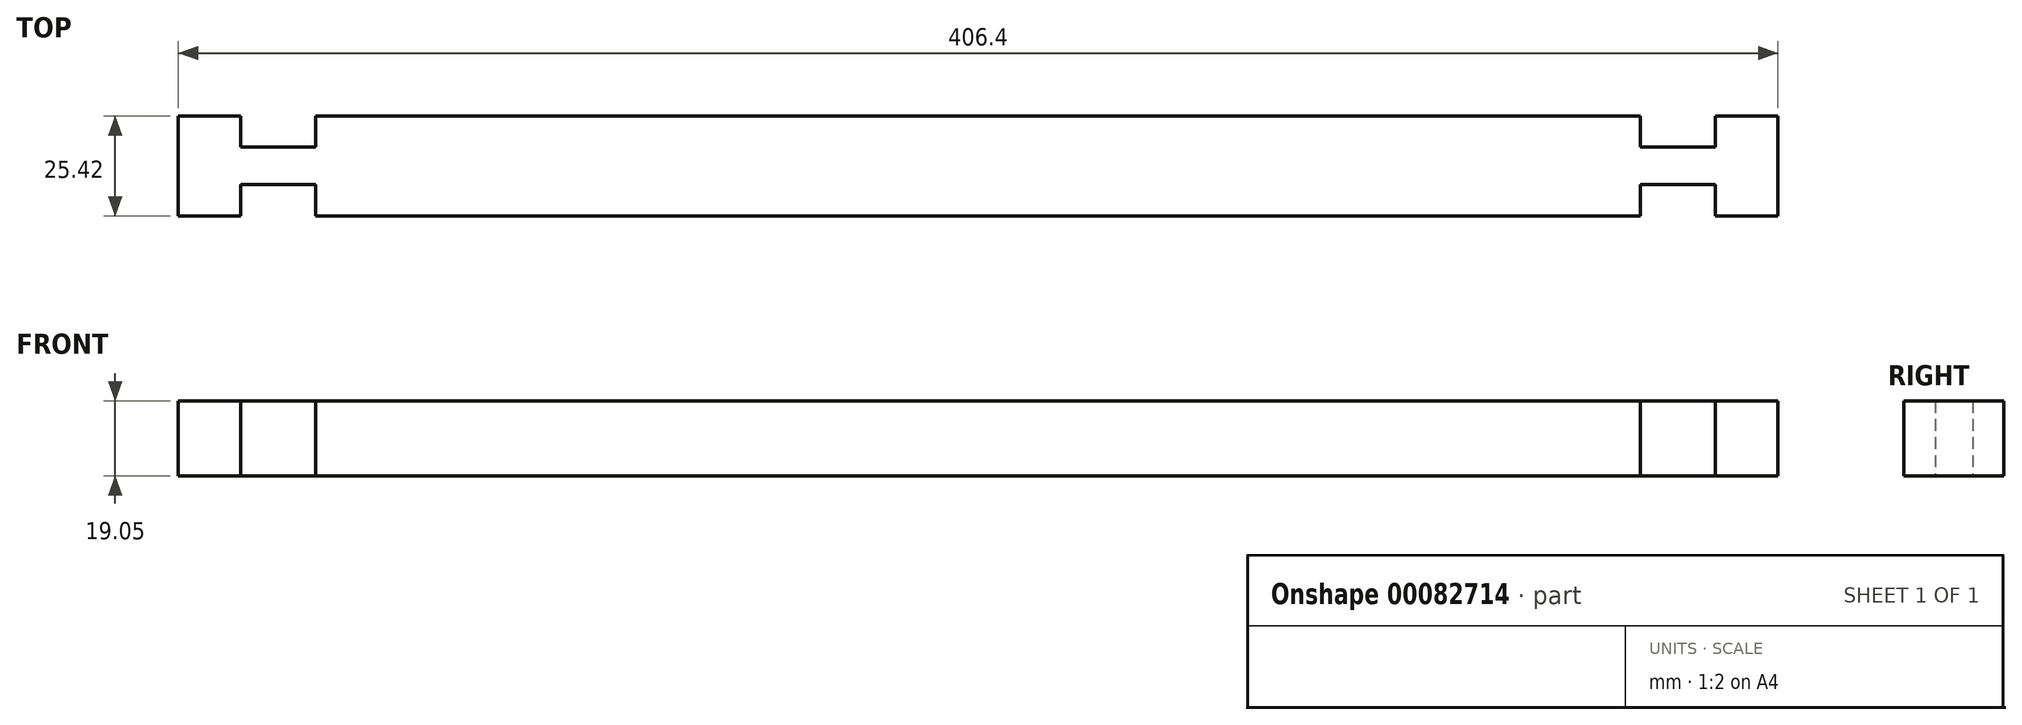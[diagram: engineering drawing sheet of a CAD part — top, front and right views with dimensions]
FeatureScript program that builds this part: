
annotation { "Feature Type Name" : "Feature", "Feature Type Description" : "" }
export const myFeature = defineFeature(function(context is Context, id is Id, definition is map)
    precondition{}
    {
        {
            var Q0;
            Q0=qCreatedBy(makeId("Top.planeOp"),FACE);
            var sketch = newSketch(context, id + "F0", { "sketchPlane" : qUnion([Q0])});
            skLineSegment(sketch, "E0", {"start": v(3.6, 15.79) * mm, "end": v(19.48, 15.79) * mm});
            skLineSegment(sketch, "E1", {"start": v(19.48, 15.79) * mm, "end": v(19.48, 23.73) * mm});
            skLineSegment(sketch, "E2", {"start": v(19.48, 23.73) * mm, "end": v(38.53, 23.73) * mm});
            skLineSegment(sketch, "E3", {"start": v(38.53, 23.73) * mm, "end": v(38.53, 15.78) * mm});
            skLineSegment(sketch, "E4", {"start": v(38.53, 15.78) * mm, "end": v(375.08, 15.78) * mm});
            skLineSegment(sketch, "E5", {"start": v(375.08, 15.78) * mm, "end": v(375.08, 23.73) * mm});
            skLineSegment(sketch, "E6", {"start": v(375.08, 23.73) * mm, "end": v(394.13, 23.73) * mm});
            skLineSegment(sketch, "E7", {"start": v(394.13, 23.73) * mm, "end": v(394.13, 15.78) * mm});
            skLineSegment(sketch, "E8", {"start": v(3.6, 15.79) * mm, "end": v(3.6, 28.49) * mm});
            skLineSegment(sketch, "E9", {"start": v(3.6, 41.19) * mm, "end": v(3.6, 28.49) * mm});
            skLineSegment(sketch, "E10.MirrorCS", {"start": v(19.48, 33.25) * mm, "end": v(38.53, 33.25) * mm});
            skLineSegment(sketch, "E11.MirrorCS", {"start": v(38.53, 33.25) * mm, "end": v(38.53, 41.2) * mm});
            skLineSegment(sketch, "E12.MirrorCS", {"start": v(19.48, 41.19) * mm, "end": v(19.48, 33.25) * mm});
            skLineSegment(sketch, "E13.MirrorCS", {"start": v(3.6, 41.19) * mm, "end": v(19.48, 41.19) * mm});
            skLineSegment(sketch, "E14", {"start": v(394.13, 15.78) * mm, "end": v(410, 15.78) * mm});
            skLineSegment(sketch, "E15", {"start": v(410, 15.78) * mm, "end": v(410, 28.49) * mm});
            skLineSegment(sketch, "E16", {"start": v(410, 28.49) * mm, "end": v(410, 41.19) * mm});
            skLineSegment(sketch, "E17.MirrorCS", {"start": v(375.08, 33.25) * mm, "end": v(394.13, 33.25) * mm});
            skLineSegment(sketch, "E18.MirrorCS", {"start": v(375.08, 41.2) * mm, "end": v(375.08, 33.25) * mm});
            skLineSegment(sketch, "E19.MirrorCS", {"start": v(394.13, 33.25) * mm, "end": v(394.13, 41.2) * mm});
            skLineSegment(sketch, "E20.MirrorCS", {"start": v(394.13, 41.2) * mm, "end": v(410, 41.2) * mm});
            skLineSegment(sketch, "E21.MirrorCS", {"start": v(38.53, 41.2) * mm, "end": v(375.08, 41.2) * mm});
            skLineSegment(sketch, "E22", {"start": v(3.6, 41.19) * mm, "end": v(3.6, 15.79) * mm});
            skLineSegment(sketch, "E23", {"start": v(410, 28.49) * mm, "end": v(410, 15.78) * mm});
            skLineSegment(sketch, "E24", {"start": v(394.13, 15.78) * mm, "end": v(394.13, 23.73) * mm});
            skLineSegment(sketch, "E25", {"start": v(375.08, 23.73) * mm, "end": v(375.08, 15.78) * mm});
            skLineSegment(sketch, "E26", {"start": v(38.53, 15.78) * mm, "end": v(38.53, 23.73) * mm});
            skLineSegment(sketch, "E27", {"start": v(19.48, 23.73) * mm, "end": v(19.48, 15.79) * mm});
            skLineSegment(sketch, "E28", {"start": v(38.53, 41.2) * mm, "end": v(38.53, 33.25) * mm});
            skLineSegment(sketch, "E29", {"start": v(410, 41.2) * mm, "end": v(410, 15.78) * mm});
            skLineSegment(sketch, "E30", {"start": v(3.6, 41.19) * mm, "end": v(410, 41.2) * mm, "construction": true});
            skSolve(sketch);
        }
        {
            var Q0;
            Q0=makeQuery(id+"F0.imprint","IMPRINT",FACE,{"disambiguationData":[TD([[makeQuery(id+"F0.imprint","IMPRINT",EDGE,{"derivedFrom":sQuery(id+"F0.wireOp",EDGE,"E2")}),1.0]])]});
            extrude(context, id + "F1", {"entities" : qUnion([Q0]), "depth" : 19.05 * mm});
        }
    });
